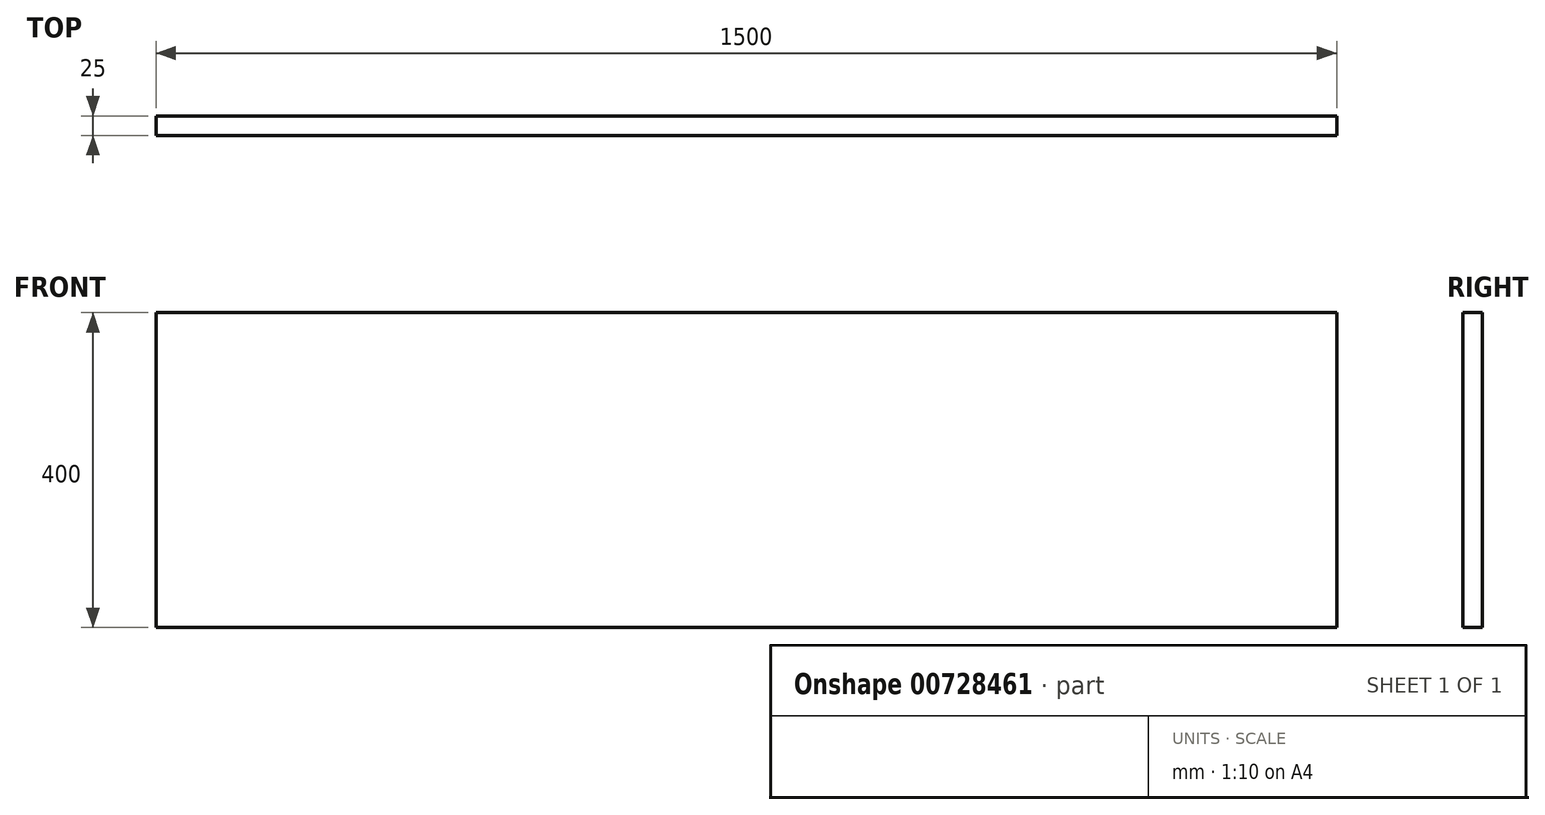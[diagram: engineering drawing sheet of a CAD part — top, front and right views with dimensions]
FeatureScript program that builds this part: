
annotation { "Feature Type Name" : "Feature", "Feature Type Description" : "" }
export const myFeature = defineFeature(function(context is Context, id is Id, definition is map)
    precondition{}
    {
        {
            var Q0;
            Q0=qCreatedBy(makeId("Front.planeOp"),FACE);
            var sketch = newSketch(context, id + "F0", { "sketchPlane" : qUnion([Q0])});
            skLineSegment(sketch, "E0.bottom", {"start": v(0, 0) * mm, "end": v(1500, 0) * mm});
            skLineSegment(sketch, "E0.top", {"start": v(0, 400) * mm, "end": v(1500, 400) * mm});
            skLineSegment(sketch, "E0.left", {"start": v(0, 0) * mm, "end": v(0, 400) * mm});
            skLineSegment(sketch, "E0.right", {"start": v(1500, 0) * mm, "end": v(1500, 400) * mm});
            skSolve(sketch);
        }
        {
            var Q0;
            Q0=makeQuery(id+"F0.imprint","IMPRINT",FACE,{"disambiguationData":[TD([[makeQuery(id+"F0.imprint","IMPRINT",EDGE,{"derivedFrom":sQuery(id+"F0.wireOp",EDGE,"E0.bottom")}),1.0]])]});
            extrude(context, id + "F1", {"entities" : qUnion([Q0]), "depth" : 25 * mm, "offsetDistance" : 25 * mm});
        }
    });
